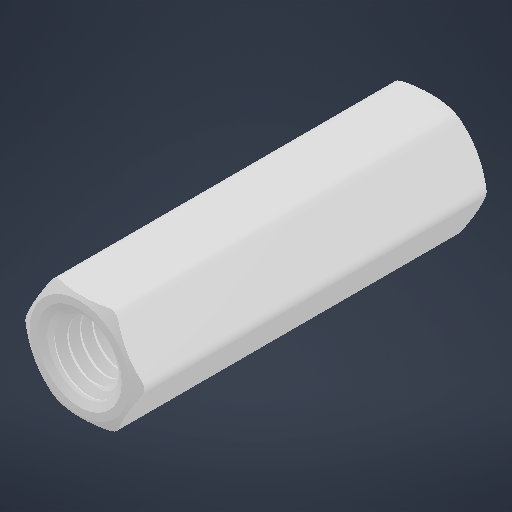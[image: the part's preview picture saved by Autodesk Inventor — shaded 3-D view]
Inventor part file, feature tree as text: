
AUTODESK INVENTOR PART (.ipt)
format: ipt  version: 2025.2 (Build 292293000, 293)  size: 587,264 bytes
history: native  units: in
note: dims shown in document units (in); Inventor stores cm internally (conversion verified against a paired STEP export)
features: other x1, mirror x1
ambient origin geometry x8: Origin, YZ Plane, XZ Plane, XY Plane, X Axis, Y Axis, Z Axis, Center Point
bodies: Solid1 (feature_tree)
feature tree (2):
  other  "Plane1"
  mirror  "Mirror1"
